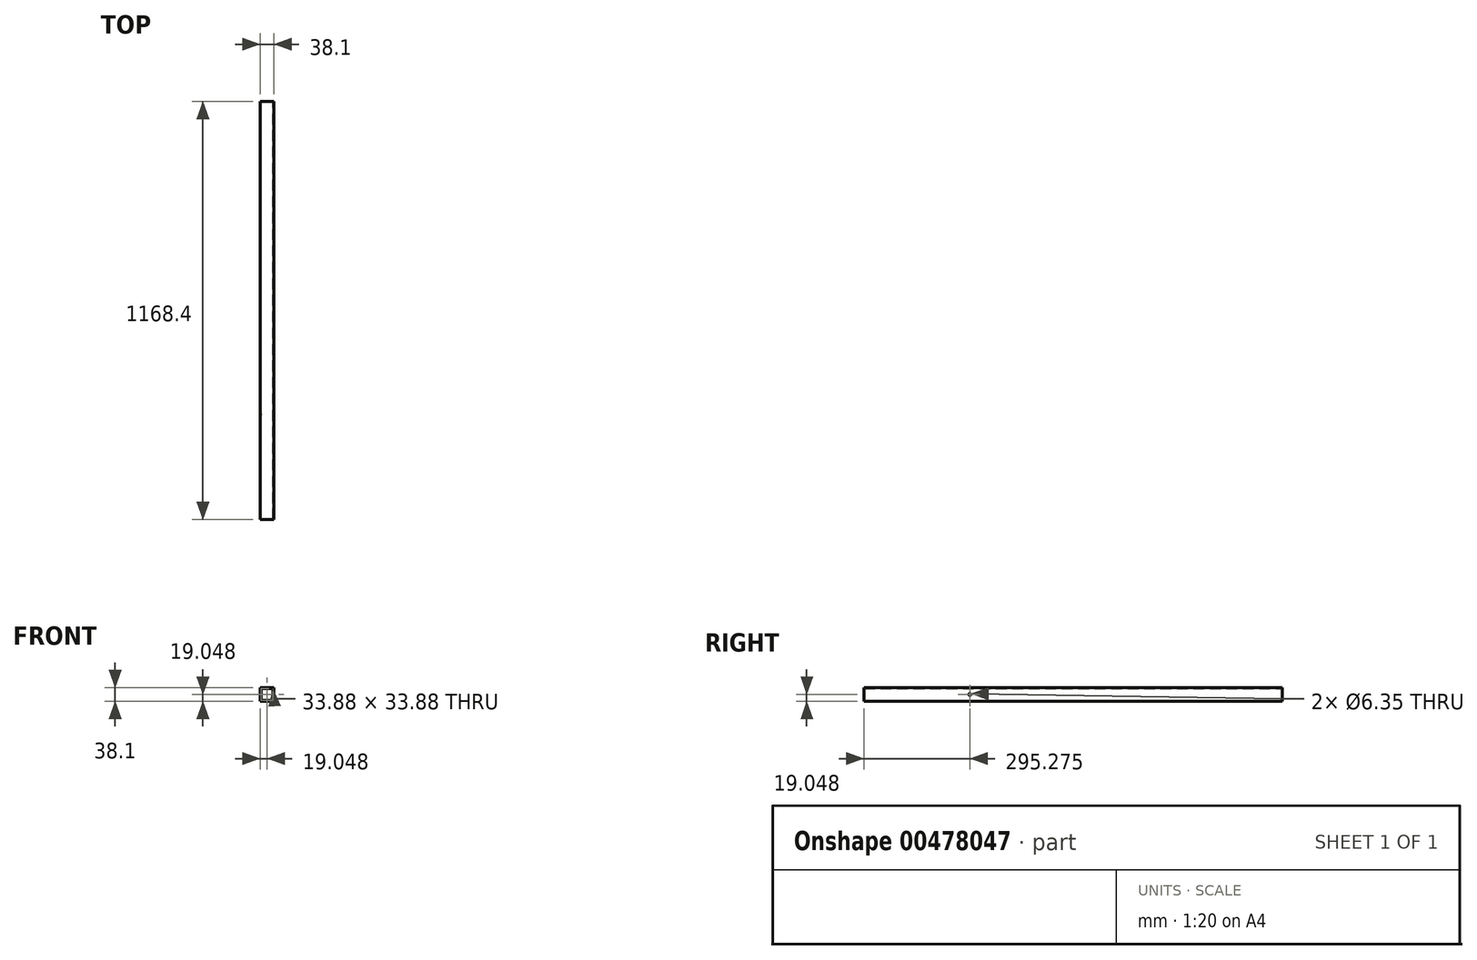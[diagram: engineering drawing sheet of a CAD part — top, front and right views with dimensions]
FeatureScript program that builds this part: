
annotation { "Feature Type Name" : "Feature", "Feature Type Description" : "" }
export const myFeature = defineFeature(function(context is Context, id is Id, definition is map)
    precondition{}
    {
        {
            var Q0;
            Q0=qCreatedBy(makeId("Front.planeOp"),FACE);
            var sketch = newSketch(context, id + "F0", { "sketchPlane" : qUnion([Q0])});
            skLineSegment(sketch, "E0.bottom", {"start": v(-54.03, 35.74) * mm, "end": v(-15.93, 35.74) * mm});
            skLineSegment(sketch, "E0.top", {"start": v(-54.03, -2.36) * mm, "end": v(-15.93, -2.36) * mm});
            skLineSegment(sketch, "E0.left", {"start": v(-54.03, 35.74) * mm, "end": v(-54.03, -2.36) * mm});
            skLineSegment(sketch, "E0.right", {"start": v(-15.93, 35.74) * mm, "end": v(-15.93, -2.36) * mm});
            skLineSegment(sketch, "E1.0", {"start": v(-18.04, 33.63) * mm, "end": v(-18.04, -0.25) * mm});
            skLineSegment(sketch, "E1.1", {"start": v(-51.92, 33.63) * mm, "end": v(-18.04, 33.63) * mm});
            skLineSegment(sketch, "E1.2", {"start": v(-51.92, 33.63) * mm, "end": v(-51.92, -0.25) * mm});
            skLineSegment(sketch, "E1.3", {"start": v(-51.92, -0.25) * mm, "end": v(-18.04, -0.25) * mm});
            skSolve(sketch);
        }
        {
            var Q0;
            Q0=qSketchRegion(id+"F0",true);
            extrude(context, id + "F1", {"entities" : qUnion([Q0]), "depth" : 1168.4 * mm});
        }
        {
            var Q0;
            Q0=makeQuery(id+"F1.opExtrude","SWEPT_FACE",FACE,{"disambiguationData":[OSD([sQuery(id+"F0.wireOp",EDGE,"E0.left")])]});
            var sketch = newSketch(context, id + "F2", { "sketchPlane" : qUnion([Q0])});
            skPoint(sketch, "E2.centerSnap0", {"position": v(0, 16.69) * mm});
            skCircle(sketch, "E3", {"center": v(873.13, 16.69) * mm, "radius": 3.17 * mm});
            skPoint(sketch, "E3.centerSnap0", {"position": v(1168.4, 16.69) * mm});
            skSolve(sketch);
        }
        {
            var Q0;
            Q0=qSketchRegion(id+"F2",true);
            extrude(context, id + "F3", {"entities" : qUnion([Q0]), "operationType" : NewBodyOperationType.REMOVE, "oppositeDirection" : true, "depth" : 76.2 * mm});
        }
    });
